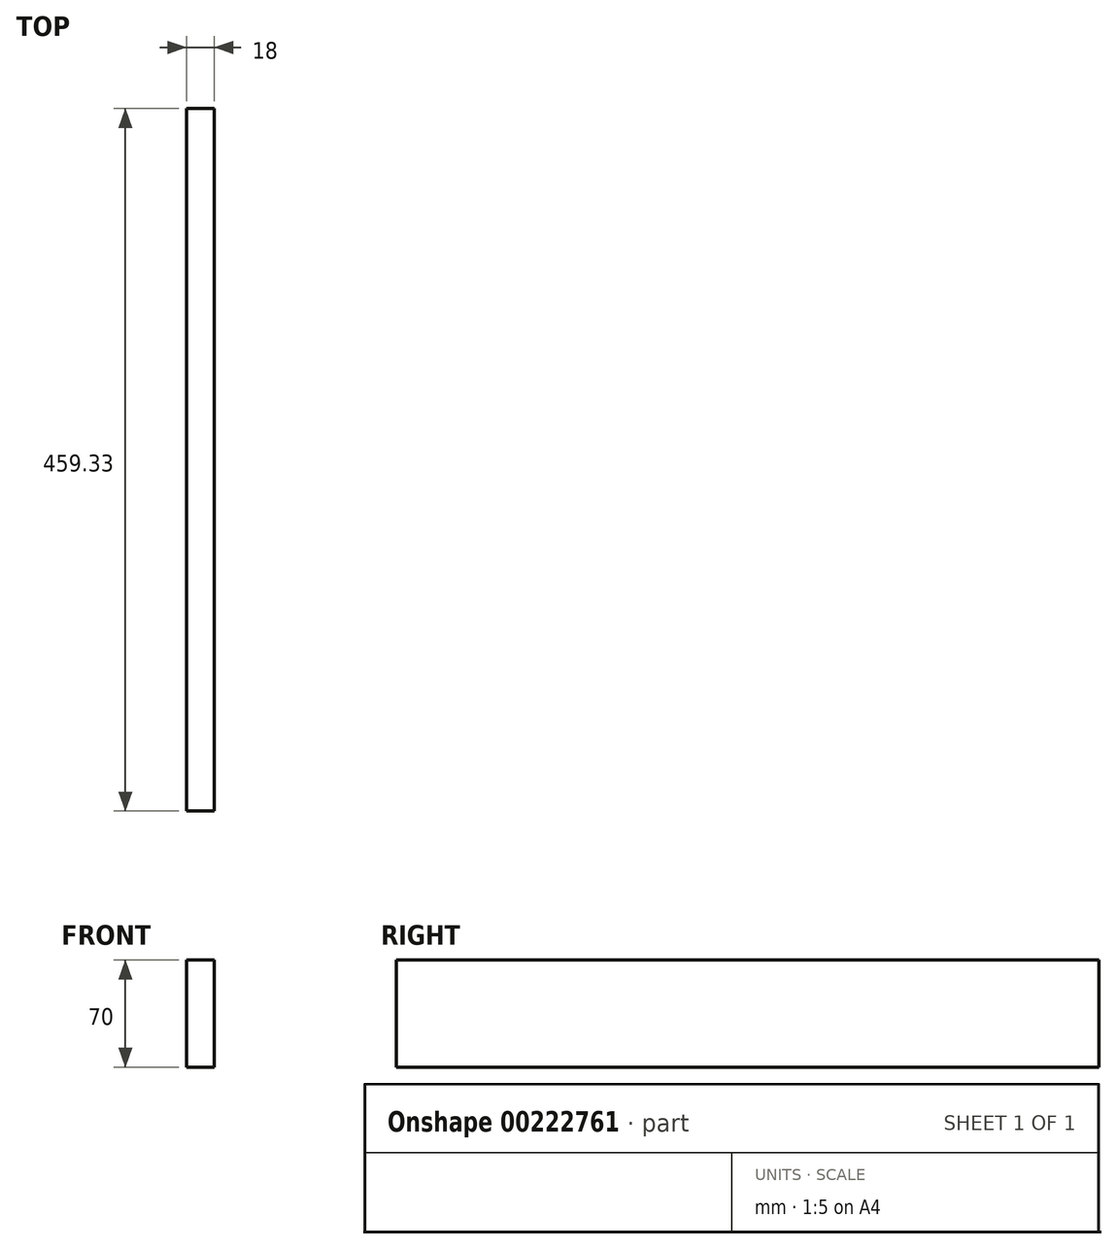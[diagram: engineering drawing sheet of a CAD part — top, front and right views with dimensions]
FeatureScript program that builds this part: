
annotation { "Feature Type Name" : "Feature", "Feature Type Description" : "" }
export const myFeature = defineFeature(function(context is Context, id is Id, definition is map)
    precondition{}
    {
        {
            var Q0;
            Q0=qCreatedBy(makeId("Right.planeOp"),FACE);
            var sketch = newSketch(context, id + "F0", { "sketchPlane" : qUnion([Q0])});
            skLineSegment(sketch, "E0.bottom", {"start": v(0, 0) * mm, "end": v(459.33, 0) * mm});
            skLineSegment(sketch, "E0.top", {"start": v(0, 70) * mm, "end": v(459.33, 70) * mm});
            skLineSegment(sketch, "E0.left", {"start": v(0, 0) * mm, "end": v(0, 70) * mm});
            skLineSegment(sketch, "E0.right", {"start": v(459.33, 0) * mm, "end": v(459.33, 70) * mm});
            skSolve(sketch);
        }
        {
            var Q0;
            Q0=makeQuery(id+"F0.imprint","IMPRINT",FACE,{"disambiguationData":[TD([[makeQuery(id+"F0.imprint","IMPRINT",EDGE,{"derivedFrom":sQuery(id+"F0.wireOp",EDGE,"E0.bottom")}),1.0]])]});
            extrude(context, id + "F1", {"entities" : qUnion([Q0]), "depth" : 18 * mm});
        }
    });
